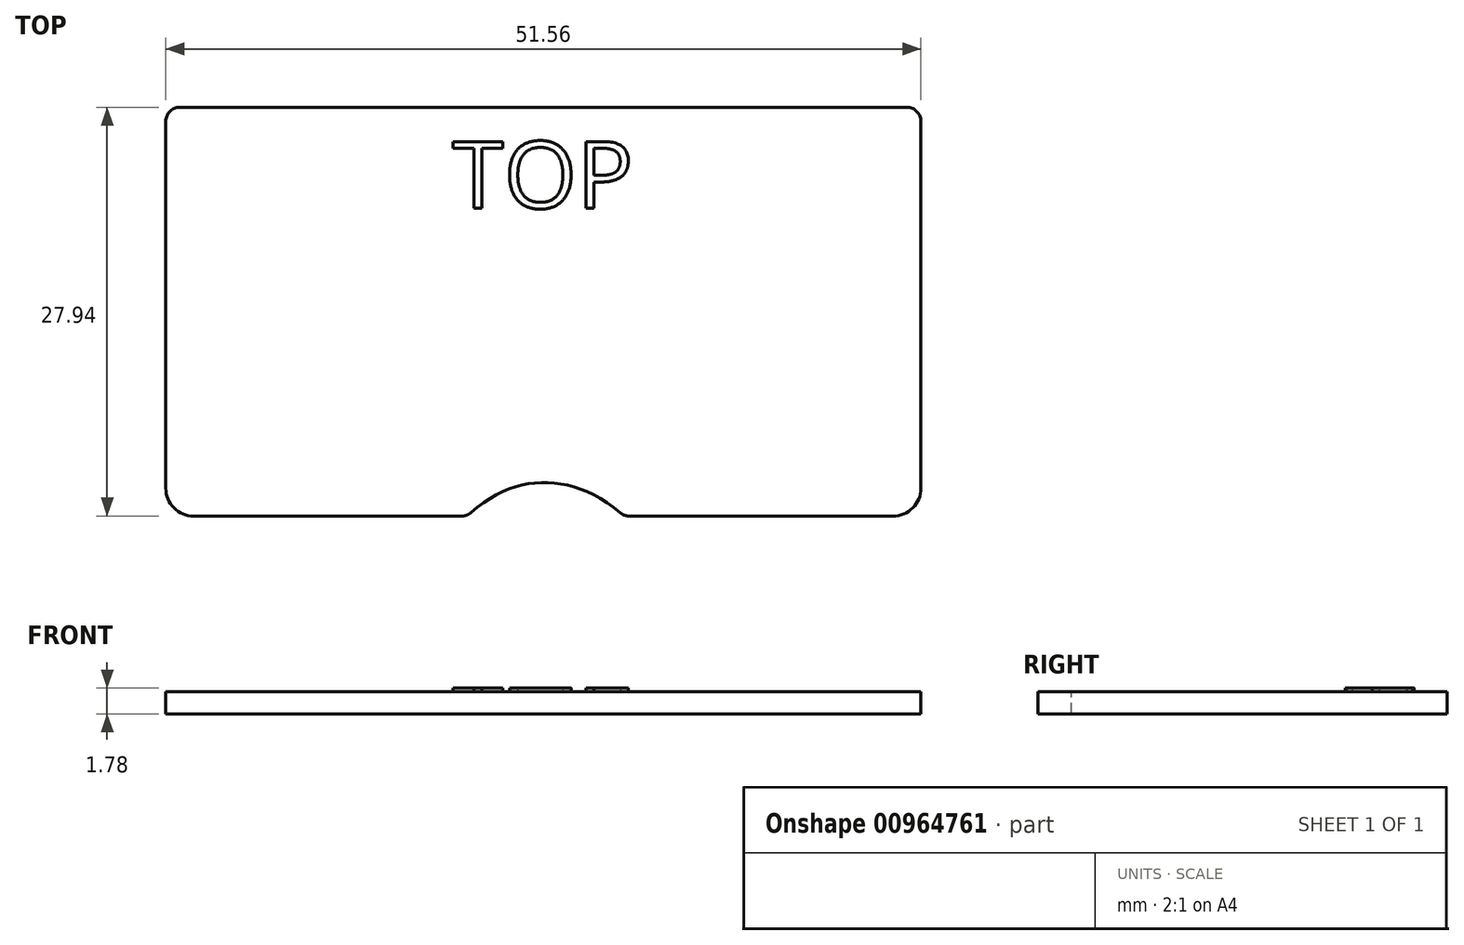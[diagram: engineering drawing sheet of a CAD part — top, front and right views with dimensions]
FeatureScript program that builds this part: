
annotation { "Feature Type Name" : "Feature", "Feature Type Description" : "" }
export const myFeature = defineFeature(function(context is Context, id is Id, definition is map)
    precondition{}
    {
        {
            var Q0;
            Q0=qCreatedBy(makeId("Top.planeOp"),FACE);
            var sketch = newSketch(context, id + "F0", { "sketchPlane" : qUnion([Q0])});
            skLineSegment(sketch, "E0.bottom", {"start": v(-25.78, -13.97) * mm, "end": v(25.78, -13.97) * mm});
            skLineSegment(sketch, "E0.top", {"start": v(-25.78, 13.97) * mm, "end": v(25.78, 13.97) * mm});
            skLineSegment(sketch, "E0.left", {"start": v(-25.78, -13.97) * mm, "end": v(-25.78, 13.97) * mm});
            skLineSegment(sketch, "E0.right", {"start": v(25.78, -13.97) * mm, "end": v(25.78, 13.97) * mm});
            skPoint(sketch, "E1", {"position": v(0, 13.97) * mm});
            skPoint(sketch, "E2", {"position": v(25.78, 0) * mm});
            skFitSpline(sketch, "E3", {"points": [v(-5.2, -13.97) * mm, v(0, -11.68) * mm, v(5.51, -13.97) * mm], "startDerivative": vector(10.4, 9.88) * mm, "endDerivative": vector(11, -9.8) * mm});
            skSolve(sketch);
        }
        {
            var Q0;
            Q0=makeQuery(id+"F0.imprint","IMPRINT",FACE,{"disambiguationData":[TD([[makeQuery(id+"F0.imprint","IMPRINT",EDGE,{"derivedFrom":sQuery(id+"F0.wireOp",EDGE,"E0.bottom")}),1.0]])]});
            extrude(context, id + "F1", {"entities" : qUnion([Q0]), "depth" : 1.52 * mm, "offsetDistance" : 25.4 * mm});
        }
        {
            var Q0;
            Q0=makeQuery(id+"F1.opExtrude","SWEPT_EDGE",EDGE,{"disambiguationData":[OSD([sQuery(id+"F0.wireOp",EDGE,"E0.top"),sQuery(id+"F0.wireOp",EDGE,"E0.left")])]});
            var Q1;
            Q1=makeQuery(id+"F1.opExtrude","SWEPT_EDGE",EDGE,{"disambiguationData":[OSD([sQuery(id+"F0.wireOp",EDGE,"E0.top"),sQuery(id+"F0.wireOp",EDGE,"E0.right")])]});
            var Q2;
            {var subQ0=sQuery(id+"F0.wireOp",EDGE,"E3");var subQ1=sQuery(id+"F0.wireOp",EDGE,"E0.bottom");Q2=makeQuery(id+"F1.opExtrude","SWEPT_EDGE",EDGE,{"disambiguationData":[OSD([subQ1,subQ0]),TDD([makeQuery(id+"F0.imprint","INTERSECT",VERTEX,{"disambiguationData":[OD(0.0)],"derivedFrom":[subQ1,subQ0]})])]});}
            var Q3;
            {var subQ0=sQuery(id+"F0.wireOp",EDGE,"E3");var subQ1=sQuery(id+"F0.wireOp",EDGE,"E0.bottom");Q3=makeQuery(id+"F1.opExtrude","SWEPT_EDGE",EDGE,{"disambiguationData":[OSD([subQ1,subQ0]),TDD([makeQuery(id+"F0.imprint","INTERSECT",VERTEX,{"disambiguationData":[OD(1.0)],"derivedFrom":[subQ1,subQ0]})])]});}
            fillet(context, id + "F2", {"entities" : qUnion([Q0, Q1, Q2, Q3]), "radius" : 0.95 * mm, "tangentPropagation" : true, "allowEdgeOverflow" : false});
        }
        {
            var Q0;
            Q0=makeQuery(id+"F1.opExtrude","SWEPT_EDGE",EDGE,{"disambiguationData":[OSD([sQuery(id+"F0.wireOp",EDGE,"E0.bottom"),sQuery(id+"F0.wireOp",EDGE,"E0.right")])]});
            var Q1;
            Q1=makeQuery(id+"F1.opExtrude","SWEPT_EDGE",EDGE,{"disambiguationData":[OSD([sQuery(id+"F0.wireOp",EDGE,"E0.bottom"),sQuery(id+"F0.wireOp",EDGE,"E0.left")])]});
            fillet(context, id + "F3", {"entities" : qUnion([Q0, Q1]), "radius" : 1.9 * mm, "tangentPropagation" : true, "allowEdgeOverflow" : false});
        }
        {
            var Q0;
            Q0=makeQuery(id+"F1.opExtrude","CAP_FACE",FACE,{"disambiguationData":[OSD([sQuery(id+"F0.wireOp",EDGE,"E0.bottom"),sQuery(id+"F0.wireOp",EDGE,"E0.top"),sQuery(id+"F0.wireOp",EDGE,"E0.left"),sQuery(id+"F0.wireOp",EDGE,"E0.right")])],"isStart":false});
            var sketch = newSketch(context, id + "F4", { "sketchPlane" : qUnion([Q0])});
            skText(sketch, "E4", { "text": "TOP", "fontName": "OpenSans-Regular.ttf"});
            skPoint(sketch, "E5", {"position": v(0, 7.07) * mm});
            const initialGuessF4  = {"E4": [-0.00623, 0.00707, 1, 0, 0.0046]};
            skSetInitialGuess(sketch, initialGuessF4);
            skSolve(sketch);
        }
        {
            var Q0;
            Q0 = qSketchRegion(id + "F4", true);
            extrude(context, id + "F5", {"entities" : qUnion([Q0]), "operationType" : NewBodyOperationType.ADD, "depth" : 0.25 * mm, "offsetDistance" : 25.4 * mm});
        }
    });
